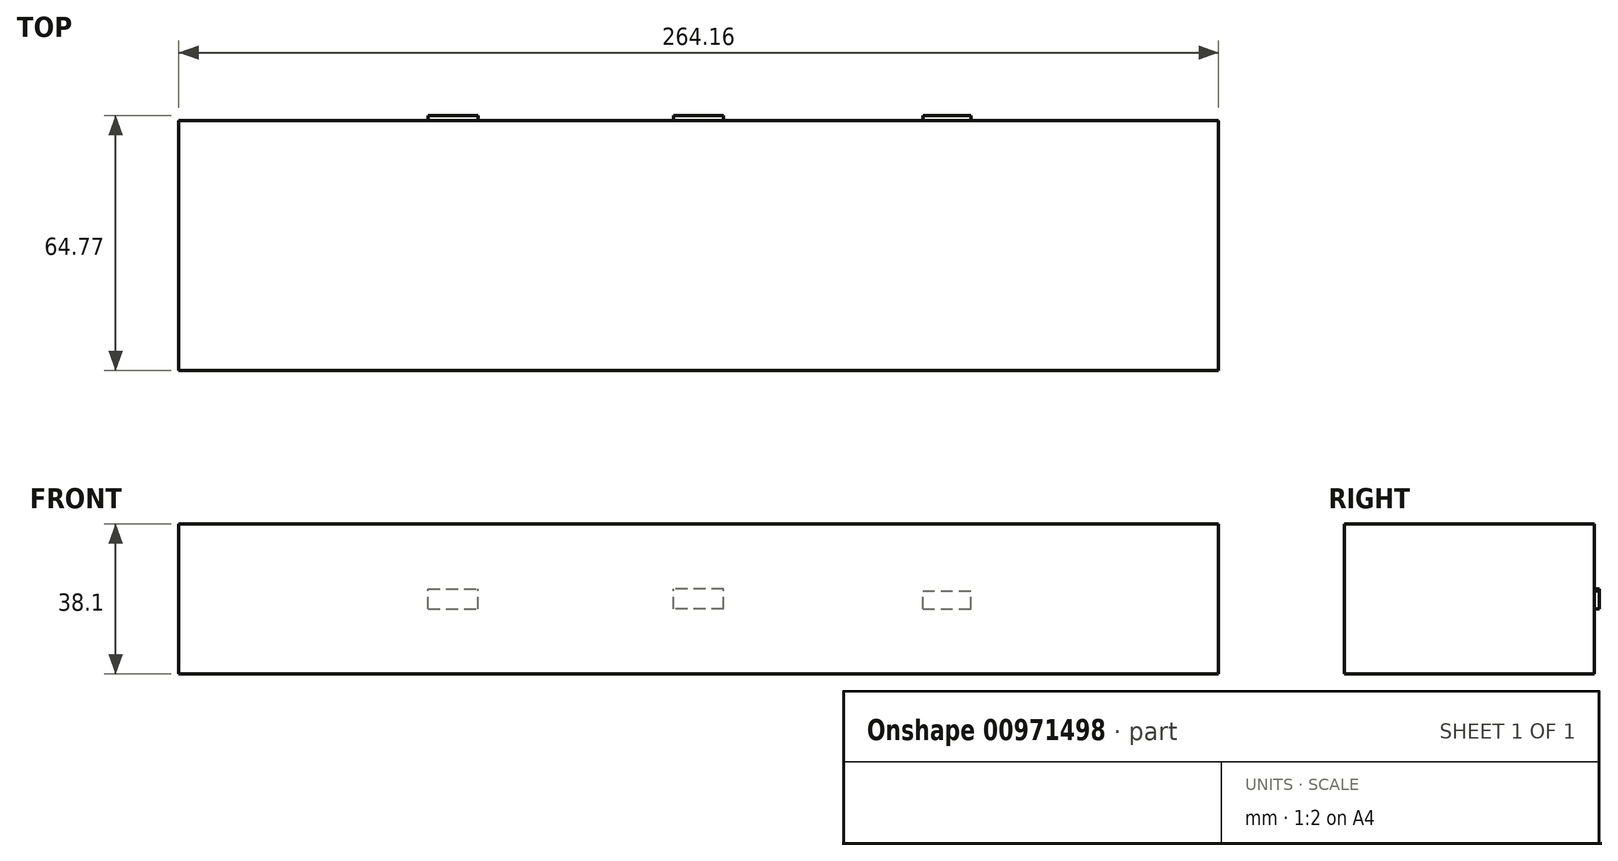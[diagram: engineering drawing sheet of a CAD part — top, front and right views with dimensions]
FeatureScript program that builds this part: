
annotation { "Feature Type Name" : "Feature", "Feature Type Description" : "" }
export const myFeature = defineFeature(function(context is Context, id is Id, definition is map)
    precondition{}
    {
        {
            var Q0;
            Q0=qCreatedBy(makeId("Right.planeOp"),FACE);
            var sketch = newSketch(context, id + "F0", { "sketchPlane" : qUnion([Q0])});
            skLineSegment(sketch, "E0.bottom", {"start": v(-31.75, 19.05) * mm, "end": v(31.75, 19.05) * mm});
            skLineSegment(sketch, "E0.top", {"start": v(-31.75, -19.05) * mm, "end": v(31.75, -19.05) * mm});
            skLineSegment(sketch, "E0.left", {"start": v(-31.75, 19.05) * mm, "end": v(-31.75, -19.05) * mm});
            skLineSegment(sketch, "E0.right", {"start": v(31.75, 19.05) * mm, "end": v(31.75, -19.05) * mm});
            skPoint(sketch, "E0.middle", {"position": v(0, 0) * mm});
            skSolve(sketch);
        }
        {
            var Q0;
            Q0=makeQuery(id+"F0.imprint","IMPRINT",FACE,{"disambiguationData":[TD([[makeQuery(id+"F0.imprint","IMPRINT",EDGE,{"derivedFrom":sQuery(id+"F0.wireOp",EDGE,"E0.bottom")}),-1.0]])]});
            extrude(context, id + "F1", {"entities" : qUnion([Q0]), "endBound" : BoundingType.SYMMETRIC, "depth" : 264.16 * mm, "offsetDistance" : 25.4 * mm});
        }
        {
            var Q0;
            Q0=makeQuery(id+"F1.opExtrude","SWEPT_FACE",FACE,{"disambiguationData":[OSD([sQuery(id+"F0.wireOp",EDGE,"E0.right")])]});
            var sketch = newSketch(context, id + "F2", { "sketchPlane" : qUnion([Q0])});
            skLineSegment(sketch, "E1.bottom", {"start": v(-56.94, -2.51) * mm, "end": v(-69.13, -2.51) * mm});
            skLineSegment(sketch, "E1.top", {"start": v(-56.94, 2.06) * mm, "end": v(-69.13, 2.06) * mm});
            skLineSegment(sketch, "E1.left", {"start": v(-56.94, -2.51) * mm, "end": v(-56.94, 2.06) * mm});
            skLineSegment(sketch, "E1.right", {"start": v(-69.13, -2.51) * mm, "end": v(-69.13, 2.06) * mm});
            skPoint(sketch, "E1.middle", {"position": v(-63.03, -0.23) * mm});
            skLineSegment(sketch, "E2.MirrorCS", {"start": v(-6.33, -2.51) * mm, "end": v(6.37, -2.51) * mm});
            skLineSegment(sketch, "E3.MirrorCS", {"start": v(-6.33, -2.51) * mm, "end": v(-6.33, 2.06) * mm});
            skLineSegment(sketch, "E4.MirrorCS", {"start": v(-6.33, 2.57) * mm, "end": v(5.86, 2.57) * mm});
            skLineSegment(sketch, "E5.MirrorCS", {"start": v(6.37, -2.51) * mm, "end": v(6.37, 2.57) * mm});
            skPoint(sketch, "E6.MirrorP", {"position": v(0.02, 0.03) * mm});
            skLineSegment(sketch, "E7.MirrorCS", {"start": v(68.73, 2.57) * mm, "end": v(56.03, 2.57) * mm});
            skLineSegment(sketch, "E8.MirrorCS", {"start": v(56.03, -2.51) * mm, "end": v(56.03, 2.57) * mm});
            skLineSegment(sketch, "E9.MirrorCS", {"start": v(68.73, -2.51) * mm, "end": v(68.73, 2.57) * mm});
            skLineSegment(sketch, "E10.MirrorCS", {"start": v(68.73, -2.51) * mm, "end": v(56.03, -2.51) * mm});
            skPoint(sketch, "E11.MirrorP", {"position": v(62.38, 0.03) * mm});
            skLineSegment(sketch, "E12.MirrorCS", {"start": v(68.23, 2.57) * mm, "end": v(56.03, 2.57) * mm});
            skLineSegment(sketch, "E13.MirrorCS", {"start": v(56.03, -2.51) * mm, "end": v(56.03, 2.06) * mm});
            skLineSegment(sketch, "E14", {"start": v(-6.33, 2.57) * mm, "end": v(-6.33, 2.06) * mm});
            skLineSegment(sketch, "E15", {"start": v(5.86, 2.57) * mm, "end": v(6.37, 2.57) * mm});
            skSolve(sketch);
        }
        {
            var Q0;
            Q0=qSketchRegion(id+"F2",true);
            extrude(context, id + "F3", {"entities" : qUnion([Q0]), "operationType" : NewBodyOperationType.ADD, "depth" : 1.27 * mm, "offsetDistance" : 25.4 * mm});
        }
    });
